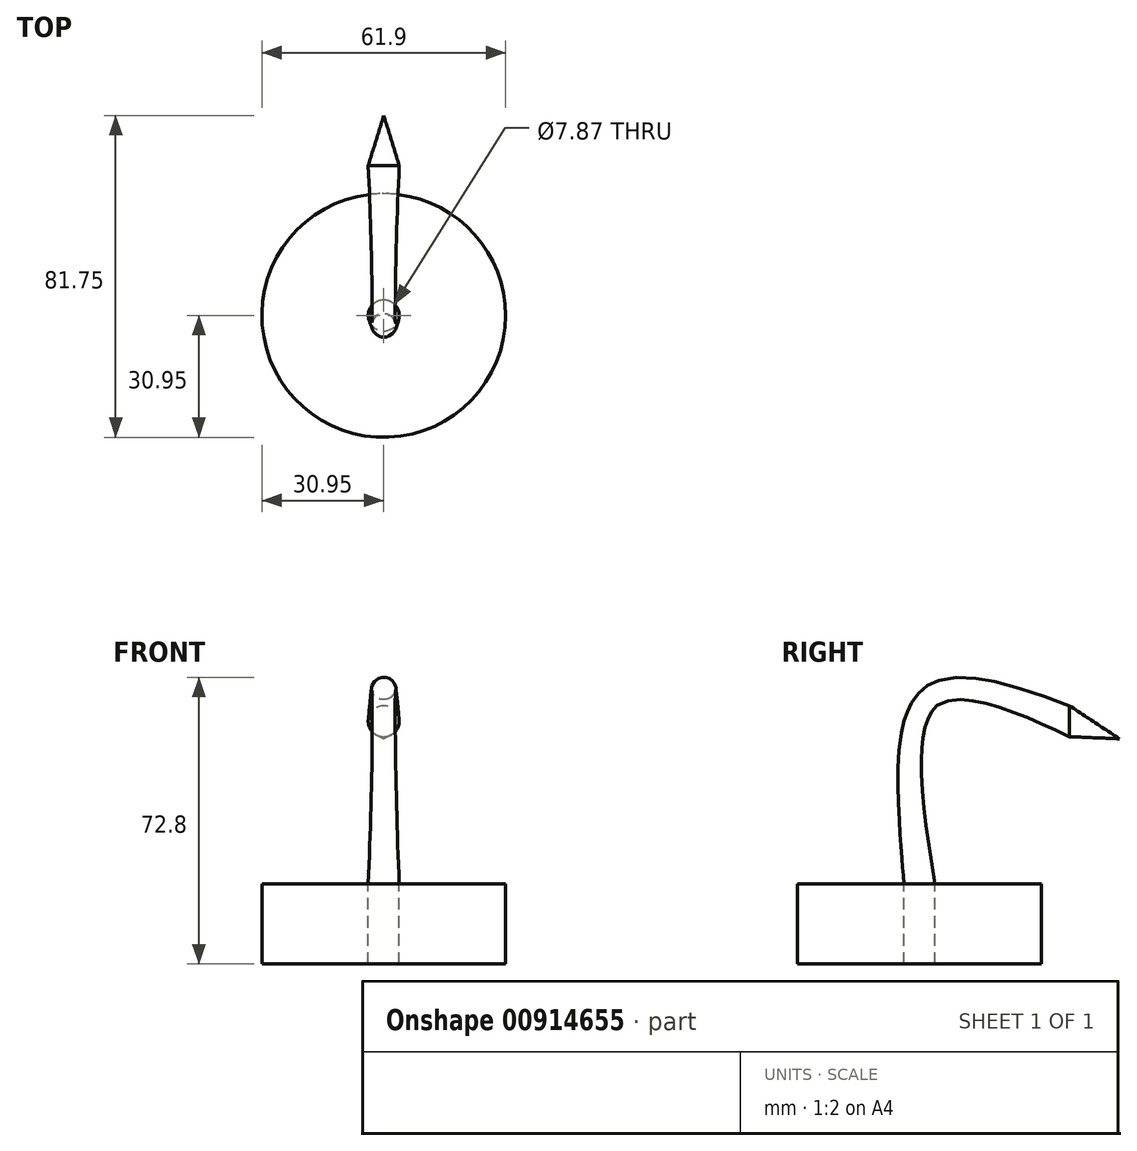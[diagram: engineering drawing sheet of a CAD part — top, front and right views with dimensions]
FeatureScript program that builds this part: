
annotation { "Feature Type Name" : "Feature", "Feature Type Description" : "" }
export const myFeature = defineFeature(function(context is Context, id is Id, definition is map)
    precondition{}
    {
        {
            var Q0;
            Q0=qCreatedBy(makeId("Top.planeOp"),FACE);
            var sketch = newSketch(context, id + "F0", { "sketchPlane" : qUnion([Q0])});
            skCircle(sketch, "E0", {"center": v(0, 0) * mm, "radius": 30.95 * mm});
            skCircle(sketch, "E1", {"center": v(0, 0) * mm, "radius": 3.94 * mm});
            skSolve(sketch);
        }
        {
            var Q0;
            Q0=qCreatedBy(makeId("Front.planeOp"),FACE);
            cPlane(context, id + "F1", {"entities" : qUnion([Q0]), "cplaneType" : CPlaneType.OFFSET, "offset" : 50.8 * mm, "oppositeDirection" : true, "width" : 152.4 * mm, "height" : 152.4 * mm});
        }
        {
            var Q0;
            Q0=qCreatedBy(id+"F1.planeOp",FACE);
            var sketch = newSketch(context, id + "F2", { "sketchPlane" : qUnion([Q0])});
            skCircle(sketch, "E2", {"center": v(0, 36.88) * mm, "radius": 1.27 * mm});
            skSolve(sketch);
        }
        {
            var Q0;
            Q0=qCreatedBy(makeId("Front.planeOp"),FACE);
            cPlane(context, id + "F3", {"entities" : qUnion([Q0]), "cplaneType" : CPlaneType.OFFSET, "offset" : 38.1 * mm, "oppositeDirection" : true, "width" : 152.4 * mm, "height" : 152.4 * mm});
        }
        {
            var Q0;
            Q0=qCreatedBy(id+"F3.planeOp",FACE);
            var sketch = newSketch(context, id + "F4", { "sketchPlane" : qUnion([Q0])});
            skCircle(sketch, "E3", {"center": v(0, 41.35) * mm, "radius": 3.94 * mm});
            skSolve(sketch);
        }
        {
            var Q0;
            Q0=qCreatedBy(makeId("Right.planeOp"),FACE);
            var sketch = newSketch(context, id + "F5", { "sketchPlane" : qUnion([Q0])});
            skFitSpline(sketch, "E4", {"points": [v(0, 0) * mm, v(2.78, 48.06) * mm, v(50.92, 36.65) * mm], "startDerivative": vector(-16.76, 126.44) * mm, "endDerivative": vector(118.3, -52.73) * mm});
            skSolve(sketch);
        }
        {
            var Q0;
            Q0=sQuery(id+"F5.wireOp",EDGE,"E4");
            var Q1;
            Q1=makeQuery(id+"F0.imprint","IMPRINT",FACE,{"disambiguationData":[TD([[makeQuery(id+"F0.imprint","IMPRINT",EDGE,{"derivedFrom":sQuery(id+"F0.wireOp",EDGE,"E1")}),1.0]])]});
            var Q2;
            Q2=makeQuery(id+"F4.imprint","IMPRINT",FACE,{"disambiguationData":[TD([[makeQuery(id+"F4.imprint","IMPRINT",EDGE,{"derivedFrom":sQuery(id+"F4.wireOp",EDGE,"E3")}),1.0]])]});
            loft(context, id + "F6", {"addSections" : true, "spine" : qUnion([Q0]), "sectionCount" : 20, "sheetProfilesArray" : [{ "sheetProfileEntities" : qUnion([Q1]) }, { "sheetProfileEntities" : qUnion([Q2]) }]});
        }
        {
            var Q1;
            Q1=makeQuery(id+"F6.opLoft","CAP_FACE",FACE,{"disambiguationData":[OSD([makeQuery(id+"F4.imprint","IMPRINT",FACE,{"disambiguationData":[TD([[makeQuery(id+"F4.imprint","IMPRINT",EDGE,{"derivedFrom":sQuery(id+"F4.wireOp",EDGE,"E3")}),1.0]])]})])],"isStart":true});
            var Q2;
            Q2=sQuery(id+"F2.wireOp",VERTEX,"E2.center");
            loft(context, id + "F7", {"operationType" : NewBodyOperationType.ADD, "sheetProfilesArray" : [{ "sheetProfileEntities" : qUnion([Q1]) }, { "sheetProfileEntities" : qUnion([Q2]) }]});
        }
        {
            var Q0;
            Q0 = qSketchRegion(id + "F0", true);
            extrude(context, id + "F8", {"entities" : qUnion([Q0]), "oppositeDirection" : true, "depth" : 20.32 * mm, "offsetDistance" : 25.4 * mm});
        }
        {
            var Q0;
            Q0=makeQuery(id+"F6.opLoft","CAP_FACE",FACE,{"disambiguationData":[OSD([makeQuery(id+"F0.imprint","IMPRINT",FACE,{"disambiguationData":[TD([[makeQuery(id+"F0.imprint","IMPRINT",EDGE,{"derivedFrom":sQuery(id+"F0.wireOp",EDGE,"E1")}),1.0]])]})])],"isStart":true});
            extrude(context, id + "F9", {"entities" : qUnion([Q0]), "depth" : 20.32 * mm, "offsetDistance" : 25.4 * mm});
        }
    });
